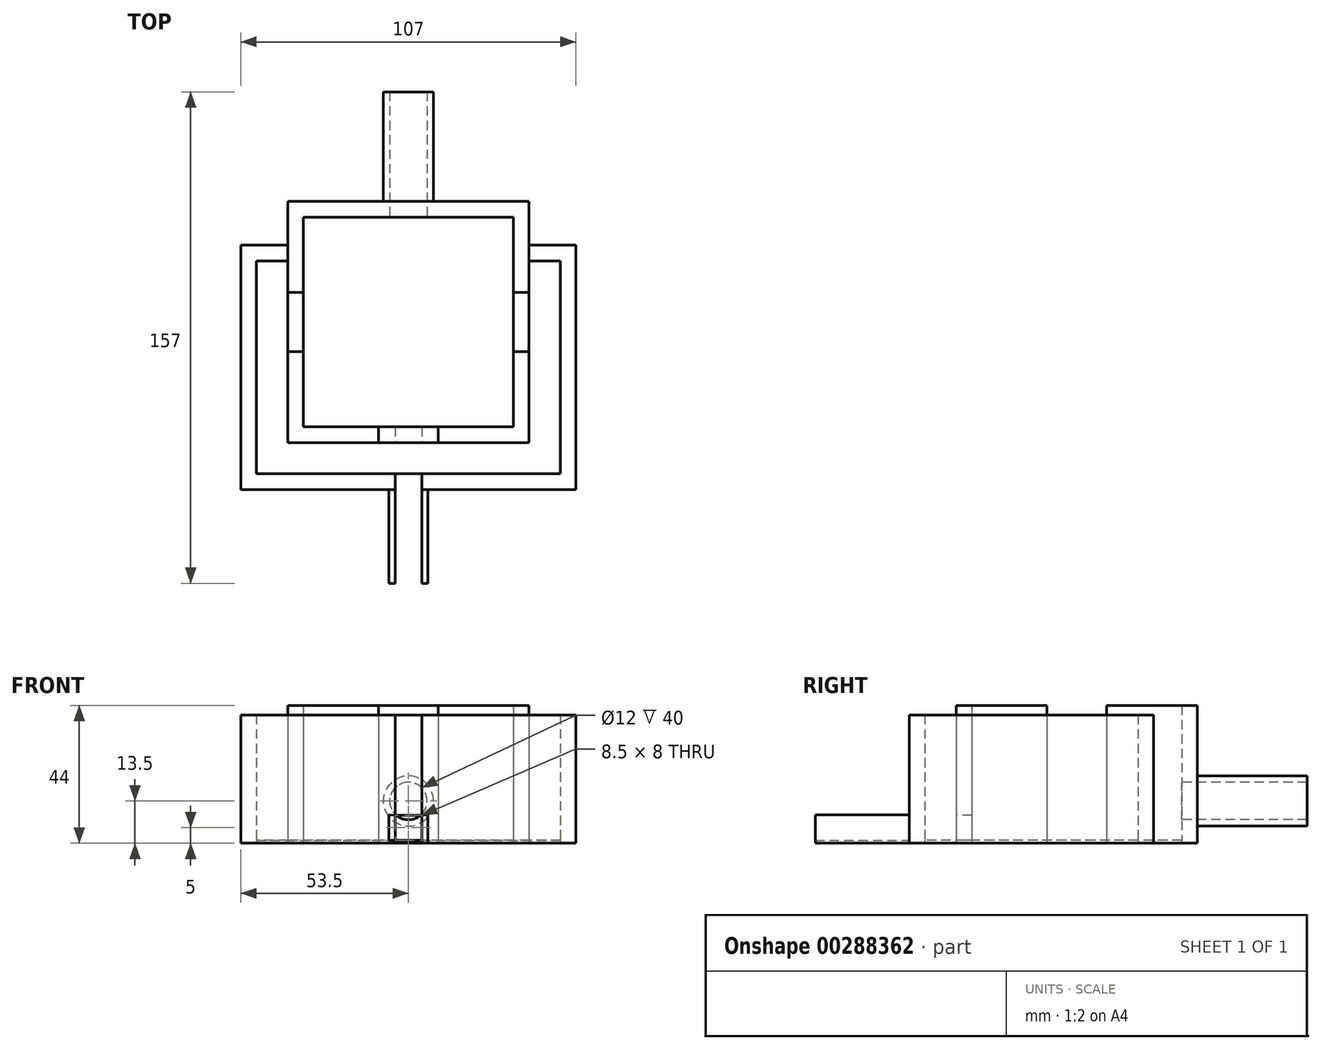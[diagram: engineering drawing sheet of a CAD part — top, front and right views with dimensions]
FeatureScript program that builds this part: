
annotation { "Feature Type Name" : "Feature", "Feature Type Description" : "" }
export const myFeature = defineFeature(function(context is Context, id is Id, definition is map)
    precondition{}
    {
        {
            var Q0;
            Q0=qCreatedBy(makeId("Top.planeOp"),FACE);
            var sketch = newSketch(context, id + "F0", { "sketchPlane" : qUnion([Q0])});
            skLineSegment(sketch, "E0.bottom", {"start": v(33.5, 33.5) * mm, "end": v(-33.5, 33.5) * mm});
            skLineSegment(sketch, "E0.top", {"start": v(33.5, -33.5) * mm, "end": v(-33.5, -33.5) * mm});
            skLineSegment(sketch, "E0.left", {"start": v(33.5, 33.5) * mm, "end": v(33.5, -33.5) * mm});
            skLineSegment(sketch, "E0.right", {"start": v(-33.5, 33.5) * mm, "end": v(-33.5, -33.5) * mm});
            skPoint(sketch, "E0.middle", {"position": v(0, 0) * mm});
            skLineSegment(sketch, "E1.0", {"start": v(38.5, -38.5) * mm, "end": v(-38.5, -38.5) * mm});
            skLineSegment(sketch, "E1.1", {"start": v(38.5, 38.5) * mm, "end": v(38.5, -38.5) * mm});
            skLineSegment(sketch, "E1.2", {"start": v(38.5, 38.5) * mm, "end": v(-38.5, 38.5) * mm});
            skLineSegment(sketch, "E1.3", {"start": v(-38.5, 38.5) * mm, "end": v(-38.5, -38.5) * mm});
            skLineSegment(sketch, "E2", {"start": v(0, 33.5) * mm, "end": v(0, -33.5) * mm, "construction": true});
            skLineSegment(sketch, "E3", {"start": v(-33.5, 0) * mm, "end": v(33.5, 0) * mm, "construction": true});
            skLineSegment(sketch, "E4.bottom", {"start": v(9.5, 9.5) * mm, "end": v(-9.5, 9.5) * mm, "construction": true});
            skLineSegment(sketch, "E4.top", {"start": v(9.5, -9.5) * mm, "end": v(-9.5, -9.5) * mm, "construction": true});
            skLineSegment(sketch, "E4.left", {"start": v(9.5, 9.5) * mm, "end": v(9.5, -9.5) * mm, "construction": true});
            skLineSegment(sketch, "E4.right", {"start": v(-9.5, 9.5) * mm, "end": v(-9.5, -9.5) * mm, "construction": true});
            skLineSegment(sketch, "E5", {"start": v(9.5, 38.5) * mm, "end": v(9.5, 33.5) * mm, "construction": true});
            skLineSegment(sketch, "E6", {"start": v(33.5, 9.5) * mm, "end": v(38.5, 9.5) * mm});
            skLineSegment(sketch, "E7", {"start": v(-38.5, 9.5) * mm, "end": v(-33.5, 9.5) * mm});
            skLineSegment(sketch, "E8", {"start": v(9.5, -33.5) * mm, "end": v(9.5, -38.5) * mm});
            skLineSegment(sketch, "E9.MirrorCS", {"start": v(-9.5, 38.5) * mm, "end": v(-9.5, 33.5) * mm, "construction": true});
            skLineSegment(sketch, "E10.MirrorCS", {"start": v(-9.5, -33.5) * mm, "end": v(-9.5, -38.5) * mm});
            skLineSegment(sketch, "E11.MirrorCS", {"start": v(33.5, -9.5) * mm, "end": v(38.5, -9.5) * mm});
            skLineSegment(sketch, "E12.MirrorCS", {"start": v(-38.5, -9.5) * mm, "end": v(-33.5, -9.5) * mm});
            skLineSegment(sketch, "E13", {"start": v(-3.2, 9.5) * mm, "end": v(-3.2, 19.5) * mm});
            skLineSegment(sketch, "E14.MirrorCS", {"start": v(-3.2, -9.5) * mm, "end": v(-3.2, -19.5) * mm});
            skLineSegment(sketch, "E15", {"start": v(-38.5, 19.5) * mm, "end": v(-48.5, 19.5) * mm});
            skLineSegment(sketch, "E16", {"start": v(-48.5, 19.5) * mm, "end": v(-48.5, -48.5) * mm});
            skLineSegment(sketch, "E17", {"start": v(-48.5, -48.5) * mm, "end": v(48.5, -48.5) * mm});
            skLineSegment(sketch, "E18", {"start": v(48.5, -48.5) * mm, "end": v(48.5, 19.5) * mm});
            skLineSegment(sketch, "E19", {"start": v(48.5, 19.5) * mm, "end": v(38.5, 19.5) * mm});
            skLineSegment(sketch, "E20.bottom", {"start": v(6, 38.5) * mm, "end": v(-6, 38.5) * mm});
            skLineSegment(sketch, "E20.top", {"start": v(6, 63.5) * mm, "end": v(-6, 63.5) * mm});
            skLineSegment(sketch, "E20.left", {"start": v(6, 38.5) * mm, "end": v(6, 63.5) * mm});
            skLineSegment(sketch, "E20.right", {"start": v(-6, 38.5) * mm, "end": v(-6, 63.5) * mm});
            skPoint(sketch, "E20.middle", {"position": v(0, 51) * mm});
            skLineSegment(sketch, "E21.bottom", {"start": v(4.25, -48.5) * mm, "end": v(-4.25, -48.5) * mm});
            skLineSegment(sketch, "E21.top", {"start": v(4.25, -73.5) * mm, "end": v(-4.25, -73.5) * mm});
            skLineSegment(sketch, "E21.left", {"start": v(4.25, -48.5) * mm, "end": v(4.25, -73.5) * mm});
            skLineSegment(sketch, "E21.right", {"start": v(-4.25, -48.5) * mm, "end": v(-4.25, -73.5) * mm});
            skPoint(sketch, "E21.middle", {"position": v(0, -61) * mm});
            skLineSegment(sketch, "E22", {"start": v(-53.5, 19.5) * mm, "end": v(-53.5, -53.5) * mm});
            skLineSegment(sketch, "E23", {"start": v(-53.5, -53.5) * mm, "end": v(53.5, -53.5) * mm});
            skLineSegment(sketch, "E24", {"start": v(53.5, -53.5) * mm, "end": v(53.5, 19.5) * mm});
            skLineSegment(sketch, "E25", {"start": v(-53.5, 19.5) * mm, "end": v(-53.5, 24.5) * mm});
            skLineSegment(sketch, "E26", {"start": v(-53.5, 24.5) * mm, "end": v(-38.5, 24.5) * mm});
            skLineSegment(sketch, "E27", {"start": v(38.5, 24.5) * mm, "end": v(53.5, 24.5) * mm});
            skLineSegment(sketch, "E28", {"start": v(53.5, 24.5) * mm, "end": v(53.5, 19.5) * mm});
            skSolve(sketch);
        }
        {
            var Q0;
            {var subQ1=sQuery(id+"F0.wireOp",EDGE,"E0.bottom");Q0=makeQuery(id+"F0.imprint","IMPRINT",FACE,{"disambiguationData":[TD([[makeQuery(id+"F0.imprint","IMPRINT",EDGE,{"derivedFrom":subQ1}),-1.0]])]});}
            var Q1;
            {var subQ4=sQuery(id+"F0.wireOp",EDGE,"E10.MirrorCS");Q1=makeQuery(id+"F0.imprint","IMPRINT",FACE,{"disambiguationData":[TD([[makeQuery(id+"F0.imprint","IMPRINT",EDGE,{"derivedFrom":subQ4}),-1.0]])]});}
            var Q2;
            {var subQ3=sQuery(id+"F0.wireOp",EDGE,"E8");Q2=makeQuery(id+"F0.imprint","IMPRINT",FACE,{"disambiguationData":[TD([[makeQuery(id+"F0.imprint","IMPRINT",EDGE,{"derivedFrom":subQ3}),1.0]])]});}
            extrude(context, id + "F1", {"entities" : qUnion([Q0, Q1, Q2]), "depth" : 44 * mm});
        }
        {
            var Q0;
            {var subQ0=sQuery(id+"F0.wireOp",EDGE,"E7");Q0=makeQuery(id+"F0.imprint","IMPRINT",FACE,{"disambiguationData":[TD([[makeQuery(id+"F0.imprint","IMPRINT",EDGE,{"derivedFrom":subQ0}),-1.0]])]});}
            var Q1;
            {var subQ0=sQuery(id+"F0.wireOp",EDGE,"E6");Q1=makeQuery(id+"F0.imprint","IMPRINT",FACE,{"disambiguationData":[TD([[makeQuery(id+"F0.imprint","IMPRINT",EDGE,{"derivedFrom":subQ0}),-1.0]])]});}
            var Q2;
            {var subQ0=sQuery(id+"F0.wireOp",EDGE,"E8");Q2=makeQuery(id+"F0.imprint","IMPRINT",FACE,{"disambiguationData":[TD([[makeQuery(id+"F0.imprint","IMPRINT",EDGE,{"derivedFrom":subQ0}),-1.0]])]});}
            extrude(context, id + "F2", {"entities" : qUnion([Q0, Q1, Q2]), "depth" : 41 * mm});
        }
        {
            var Q0;
            {var subQ4=sQuery(id+"F0.wireOp",EDGE,"E15");Q0=makeQuery(id+"F0.imprint","IMPRINT",FACE,{"disambiguationData":[TD([[makeQuery(id+"F0.imprint","IMPRINT",EDGE,{"derivedFrom":subQ4}),-1.0]])]});}
            var Q1;
            {var subQ3=sQuery(id+"F0.wireOp",EDGE,"E18");Q1=makeQuery(id+"F0.imprint","IMPRINT",FACE,{"disambiguationData":[TD([[makeQuery(id+"F0.imprint","IMPRINT",EDGE,{"derivedFrom":subQ3}),-1.0]])]});}
            var Q2;
            {var subQ0=sQuery(id+"F0.wireOp",EDGE,"E21.bottom");Q2=makeQuery(id+"F0.imprint","IMPRINT",FACE,{"disambiguationData":[TD([[makeQuery(id+"F0.imprint","IMPRINT",EDGE,{"derivedFrom":subQ0}),1.0]])]});}
            extrude(context, id + "F3", {"entities" : qUnion([Q0, Q1, Q2]), "operationType" : NewBodyOperationType.ADD, "depth" : 41 * mm});
        }
        {
            var Q0;
            {var subQ7=sQuery(id+"F0.wireOp",EDGE,"E0.bottom");Q0=makeQuery(id+"F0.imprint","IMPRINT",FACE,{"disambiguationData":[TD([[makeQuery(id+"F0.imprint","IMPRINT",EDGE,{"derivedFrom":subQ7}),1.0]])]});}
            var Q1;
            {var subQ0=sQuery(id+"F0.wireOp",EDGE,"E15");Q1=makeQuery(id+"F0.imprint","IMPRINT",FACE,{"disambiguationData":[TD([[makeQuery(id+"F0.imprint","IMPRINT",EDGE,{"derivedFrom":subQ0}),1.0]])]});}
            extrude(context, id + "F4", {"entities" : qUnion([Q0, Q1]), "depth" : 1 * mm});
        }
        {
            var Q0;
            Q0=makeQuery(id+"F1.opExtrude","SWEPT_FACE",FACE,{"disambiguationData":[OSD([sQuery(id+"F0.wireOp",EDGE,"E1.2"),sQuery(id+"F0.wireOp",EDGE,"E20.bottom")])]});
            var sketch = newSketch(context, id + "F5", { "sketchPlane" : qUnion([Q0])});
            skCircle(sketch, "E29", {"center": v(0, 13.5) * mm, "radius": 6 * mm});
            skCircle(sketch, "E30.0", {"center": v(0, 13.5) * mm, "radius": 8 * mm});
            skSolve(sketch);
        }
        {
            var Q0;
            Q0=makeQuery(id+"F5.imprint","IMPRINT",FACE,{"disambiguationData":[TD([[makeQuery(id+"F5.imprint","IMPRINT",EDGE,{"derivedFrom":sQuery(id+"F5.wireOp",EDGE,"E29")}),-1.0]])]});
            extrude(context, id + "F6", {"entities" : qUnion([Q0]), "operationType" : NewBodyOperationType.ADD, "depth" : 35 * mm});
        }
        {
            var Q0;
            Q0=makeQuery(id+"F6.boolean.opBoolean","SPLIT",FACE,{"disambiguationData":[TD([makeQuery(id+"F6.opExtrude","SWEPT_FACE",FACE,{"disambiguationData":[OSD([sQuery(id+"F5.wireOp",EDGE,"E29")])]})])],"derivedFrom":makeQuery(id+"F1.opExtrude","SWEPT_FACE",FACE,{"disambiguationData":[OSD([sQuery(id+"F0.wireOp",EDGE,"E1.2"),sQuery(id+"F0.wireOp",EDGE,"E20.bottom")])]})});
            extrude(context, id + "F7", {"entities" : qUnion([Q0]), "operationType" : NewBodyOperationType.REMOVE, "oppositeDirection" : true, "depth" : 25 * mm});
        }
        {
            var Q0;
            Q0=makeQuery(id+"F3.opExtrude","SWEPT_FACE",FACE,{"disambiguationData":[OSD([sQuery(id+"F0.wireOp",EDGE,"E23")])]});
            var sketch = newSketch(context, id + "F8", { "sketchPlane" : qUnion([Q0])});
            skLineSegment(sketch, "E31.bottom", {"start": v(4.25, 0) * mm, "end": v(-4.25, 0) * mm});
            skLineSegment(sketch, "E31.top", {"start": v(4.25, 9) * mm, "end": v(-4.25, 9) * mm});
            skLineSegment(sketch, "E31.left", {"start": v(4.25, 0) * mm, "end": v(4.25, 9) * mm});
            skLineSegment(sketch, "E31.right", {"start": v(-4.25, 0) * mm, "end": v(-4.25, 9) * mm});
            skPoint(sketch, "E31.middle", {"position": v(0, 4.5) * mm});
            skLineSegment(sketch, "E32.0", {"start": v(6.25, 0) * mm, "end": v(6.25, 9.1) * mm});
            skLineSegment(sketch, "E32.2", {"start": v(-6.25, 0) * mm, "end": v(-6.25, 9.1) * mm});
            skLineSegment(sketch, "E33", {"start": v(-6.25, 9.1) * mm, "end": v(-4.25, 9) * mm});
            skLineSegment(sketch, "E34", {"start": v(4.25, 9) * mm, "end": v(6.25, 9.1) * mm});
            skLineSegment(sketch, "E35", {"start": v(-6.25, 1) * mm, "end": v(6.25, 1) * mm});
            skSolve(sketch);
        }
        {
            var Q0;
            {var subQ0=sQuery(id+"F8.wireOp",EDGE,"E31.bottom");Q0=makeQuery(id+"F8.imprint","IMPRINT",FACE,{"disambiguationData":[TD([[makeQuery(id+"F8.imprint","IMPRINT",EDGE,{"derivedFrom":subQ0}),1.0]])]});}
            var Q1;
            {var subQ0=sQuery(id+"F8.wireOp",EDGE,"E34");Q1=makeQuery(id+"F8.imprint","IMPRINT",FACE,{"disambiguationData":[TD([[makeQuery(id+"F8.imprint","IMPRINT",EDGE,{"derivedFrom":subQ0}),-1.0]])]});}
            var Q2;
            {var subQ0=sQuery(id+"F8.wireOp",EDGE,"E33");Q2=makeQuery(id+"F8.imprint","IMPRINT",FACE,{"disambiguationData":[TD([[makeQuery(id+"F8.imprint","IMPRINT",EDGE,{"derivedFrom":subQ0}),-1.0]])]});}
            var Q3;
            {var subQ1=makeQuery(id+"F3.opExtrude","CAP_EDGE",EDGE,{"disambiguationData":[OSD([sQuery(id+"F0.wireOp",EDGE,"E23")])],"isStart":true});var subQ5=sQuery(id+"F8.wireOp",EDGE,"E32.0");var subQ6=makeQuery(id+"F8.imprint","INTERSECT",VERTEX,{"derivedFrom":[subQ1,subQ5]});Q3=makeQuery(id+"F8.imprint","IMPRINT",FACE,{"disambiguationData":[TD([[makeQuery(id+"F8.imprint","IMPRINT",EDGE,{"disambiguationData":[TD([[subQ6,-1.0]])],"derivedFrom":subQ5}),1.0]])]});}
            var Q4;
            {var subQ1=makeQuery(id+"F3.opExtrude","CAP_EDGE",EDGE,{"disambiguationData":[OSD([sQuery(id+"F0.wireOp",EDGE,"E23")])],"isStart":true});var subQ5=sQuery(id+"F8.wireOp",EDGE,"E32.2");var subQ6=makeQuery(id+"F8.imprint","INTERSECT",VERTEX,{"derivedFrom":[subQ1,subQ5]});Q4=makeQuery(id+"F8.imprint","IMPRINT",FACE,{"disambiguationData":[TD([[makeQuery(id+"F8.imprint","IMPRINT",EDGE,{"disambiguationData":[TD([[subQ6,-1.0]])],"derivedFrom":subQ5}),-1.0]])]});}
            extrude(context, id + "F9", {"entities" : qUnion([Q0, Q1, Q2, Q3, Q4]), "operationType" : NewBodyOperationType.ADD, "depth" : 30 * mm});
        }
        {
            var Q0;
            {var subQ0=sQuery(id+"F8.wireOp",EDGE,"E31.top");Q0=makeQuery(id+"F8.imprint","IMPRINT",FACE,{"disambiguationData":[TD([[makeQuery(id+"F8.imprint","IMPRINT",EDGE,{"derivedFrom":subQ0}),1.0]])]});}
            extrude(context, id + "F10", {"entities" : qUnion([Q0]), "operationType" : NewBodyOperationType.REMOVE, "oppositeDirection" : true, "depth" : 25 * mm});
        }
    });
